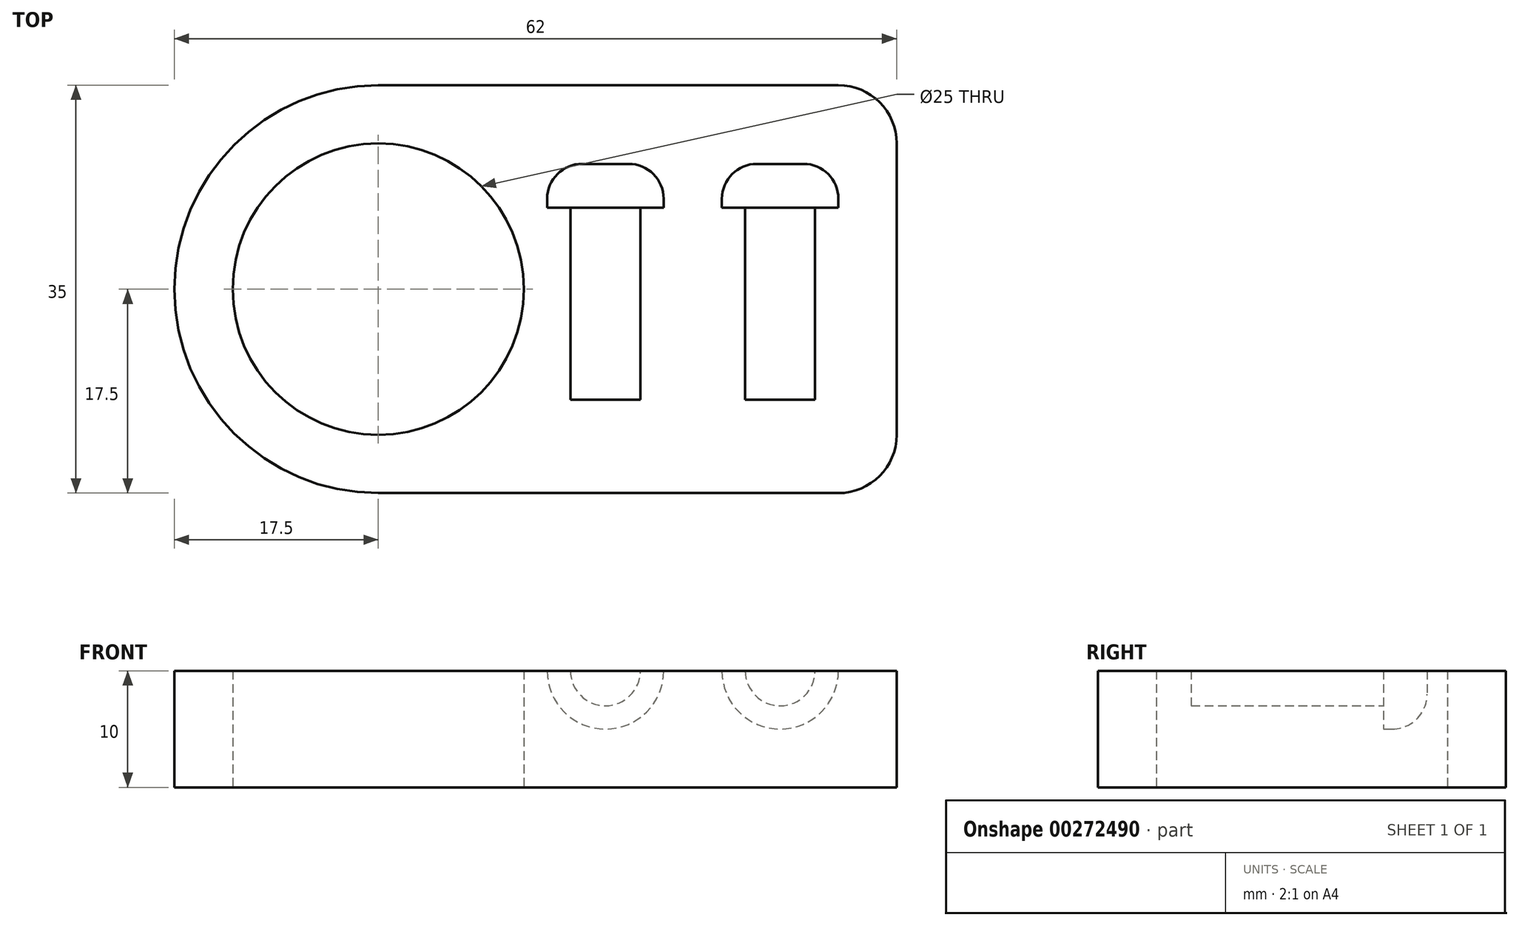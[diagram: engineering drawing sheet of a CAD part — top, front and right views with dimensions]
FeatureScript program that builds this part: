
annotation { "Feature Type Name" : "Feature", "Feature Type Description" : "" }
export const myFeature = defineFeature(function(context is Context, id is Id, definition is map)
    precondition{}
    {
        {
            var Q0;
            Q0=qCreatedBy(makeId("Top.planeOp"),FACE);
            var sketch = newSketch(context, id + "F0", { "sketchPlane" : qUnion([Q0])});
            skLineSegment(sketch, "E0.bottom", {"start": v(17.5, 0) * mm, "end": v(57, 0) * mm});
            skLineSegment(sketch, "E0.top", {"start": v(17.5, 35) * mm, "end": v(57, 35) * mm});
            skLineSegment(sketch, "E0.left", {"start": v(0, 17.5) * mm, "end": v(0, 17.5) * mm});
            skLineSegment(sketch, "E0.right", {"start": v(62, 5) * mm, "end": v(62, 30) * mm});
            skLineSegment(sketch, "E1.bottom", {"start": v(0, 0) * mm, "end": v(17.5, 0) * mm, "construction": true});
            skLineSegment(sketch, "E1.top", {"start": v(0, 17.5) * mm, "end": v(17.5, 17.5) * mm, "construction": true});
            skLineSegment(sketch, "E1.left", {"start": v(0, 0) * mm, "end": v(0, 17.5) * mm, "construction": true});
            skLineSegment(sketch, "E1.right", {"start": v(17.5, 0) * mm, "end": v(17.5, 17.5) * mm, "construction": true});
            skCircle(sketch, "E2", {"center": v(17.5, 17.5) * mm, "radius": 12.5 * mm});
            skPoint(sketch, "E3.visualSharp", {"position": v(0, 0) * mm});
            skArc(sketch, "E3.filletArc", {"start": v(0, 17.5) * mm, "mid": v(5.13, 5.13) * mm, "end": v(17.5, 0) * mm});
            skPoint(sketch, "E4.visualSharp", {"position": v(0, 35) * mm});
            skArc(sketch, "E4.filletArc", {"start": v(17.5, 35) * mm, "mid": v(5.13, 29.87) * mm, "end": v(0, 17.5) * mm});
            skPoint(sketch, "E5.visualSharp", {"position": v(62, 35) * mm});
            skArc(sketch, "E5.filletArc", {"start": v(62, 30) * mm, "mid": v(60.54, 33.54) * mm, "end": v(57, 35) * mm});
            skPoint(sketch, "E6.visualSharp", {"position": v(62, 0) * mm});
            skArc(sketch, "E6.filletArc", {"start": v(57, 0) * mm, "mid": v(60.54, 1.46) * mm, "end": v(62, 5) * mm});
            skSolve(sketch);
        }
        {
            var Q0;
            Q0=makeQuery(id+"F0.imprint","IMPRINT",FACE,{"disambiguationData":[TD([[makeQuery(id+"F0.imprint","IMPRINT",EDGE,{"derivedFrom":sQuery(id+"F0.wireOp",EDGE,"E0.bottom")}),1.0]])]});
            extrude(context, id + "F1", {"entities" : qUnion([Q0]), "depth" : 10 * mm});
        }
        {
            var Q0;
            Q0=makeQuery(id+"F1.opExtrude","CAP_FACE",FACE,{"disambiguationData":[OSD([sQuery(id+"F0.wireOp",EDGE,"E0.bottom"),sQuery(id+"F0.wireOp",EDGE,"E0.top"),sQuery(id+"F0.wireOp",EDGE,"E0.right"),sQuery(id+"F0.wireOp",EDGE,"E2"),sQuery(id+"F0.wireOp",EDGE,"E3.filletArc"),sQuery(id+"F0.wireOp",EDGE,"E4.filletArc"),sQuery(id+"F0.wireOp",EDGE,"E5.filletArc"),sQuery(id+"F0.wireOp",EDGE,"E6.filletArc")])],"isStart":false});
            var sketch = newSketch(context, id + "F2", { "sketchPlane" : qUnion([Q0])});
            skLineSegment(sketch, "E7.bottom", {"start": v(0, 0) * mm, "end": v(37, 0) * mm, "construction": true});
            skLineSegment(sketch, "E7.top", {"start": v(0, 8) * mm, "end": v(37, 8) * mm, "construction": true});
            skLineSegment(sketch, "E7.left", {"start": v(0, 0) * mm, "end": v(0, 8) * mm, "construction": true});
            skLineSegment(sketch, "E7.right", {"start": v(37, 0) * mm, "end": v(37, 8) * mm, "construction": true});
            skLineSegment(sketch, "E8.bottom", {"start": v(37, 8) * mm, "end": v(40, 8) * mm});
            skLineSegment(sketch, "E8.left", {"start": v(37, 8) * mm, "end": v(37, 24.5) * mm});
            skLineSegment(sketch, "E8.right", {"start": v(40, 8) * mm, "end": v(40, 24.5) * mm});
            skLineSegment(sketch, "E9.bottom", {"start": v(40, 24.5) * mm, "end": v(42, 24.5) * mm});
            skLineSegment(sketch, "E9.top", {"start": v(37, 28.25) * mm, "end": v(39, 28.25) * mm});
            skLineSegment(sketch, "E9.left", {"start": v(37, 24.5) * mm, "end": v(37, 28.25) * mm});
            skLineSegment(sketch, "E9.right", {"start": v(42, 24.5) * mm, "end": v(42, 25.25) * mm});
            skLineSegment(sketch, "E10", {"start": v(37, 8) * mm, "end": v(52, 8) * mm, "construction": true});
            skPoint(sketch, "E10.endSnap0", {"position": v(38.5, 8) * mm});
            skLineSegment(sketch, "E11.bottom", {"start": v(52, 8) * mm, "end": v(55, 8) * mm});
            skLineSegment(sketch, "E11.left", {"start": v(52, 8) * mm, "end": v(52, 24.5) * mm});
            skLineSegment(sketch, "E11.right", {"start": v(55, 8) * mm, "end": v(55, 24.5) * mm});
            skLineSegment(sketch, "E12.bottom", {"start": v(55, 24.5) * mm, "end": v(57, 24.5) * mm});
            skLineSegment(sketch, "E12.top", {"start": v(52, 28.25) * mm, "end": v(54, 28.25) * mm});
            skLineSegment(sketch, "E12.left", {"start": v(52, 24.5) * mm, "end": v(52, 28.25) * mm});
            skLineSegment(sketch, "E12.right", {"start": v(57, 24.5) * mm, "end": v(57, 25.25) * mm});
            skPoint(sketch, "E13.visualSharp", {"position": v(42, 28.25) * mm});
            skArc(sketch, "E13.filletArc", {"start": v(42, 25.25) * mm, "mid": v(41.12, 27.37) * mm, "end": v(39, 28.25) * mm});
            skPoint(sketch, "E14.visualSharp", {"position": v(57, 28.25) * mm});
            skArc(sketch, "E14.filletArc", {"start": v(57, 25.25) * mm, "mid": v(56.12, 27.37) * mm, "end": v(54, 28.25) * mm});
            skSolve(sketch);
        }
        {
            var Q0;
            Q0=makeQuery(id+"F2.imprint","IMPRINT",FACE,{"disambiguationData":[TD([[makeQuery(id+"F2.imprint","IMPRINT",EDGE,{"derivedFrom":sQuery(id+"F2.wireOp",EDGE,"E8.bottom")}),1.0]])]});
            var Q1;
            Q1=sQuery(id+"F2.wireOp",EDGE,"E8.left");
            revolve(context, id + "F3", {"operationType" : NewBodyOperationType.REMOVE, "entities" : qUnion([Q0]), "axis" : qUnion([Q1]), "revolveType" : RevolveType.FULL, "oppositeDirection" : true});
        }
        {
            var Q0;
            Q0=makeQuery(id+"F2.imprint","IMPRINT",FACE,{"disambiguationData":[TD([[makeQuery(id+"F2.imprint","IMPRINT",EDGE,{"derivedFrom":sQuery(id+"F2.wireOp",EDGE,"E11.bottom")}),1.0]])]});
            var Q1;
            Q1=sQuery(id+"F2.wireOp",EDGE,"E11.left");
            revolve(context, id + "F4", {"operationType" : NewBodyOperationType.REMOVE, "entities" : qUnion([Q0]), "axis" : qUnion([Q1]), "revolveType" : RevolveType.FULL, "oppositeDirection" : true});
        }
    });
